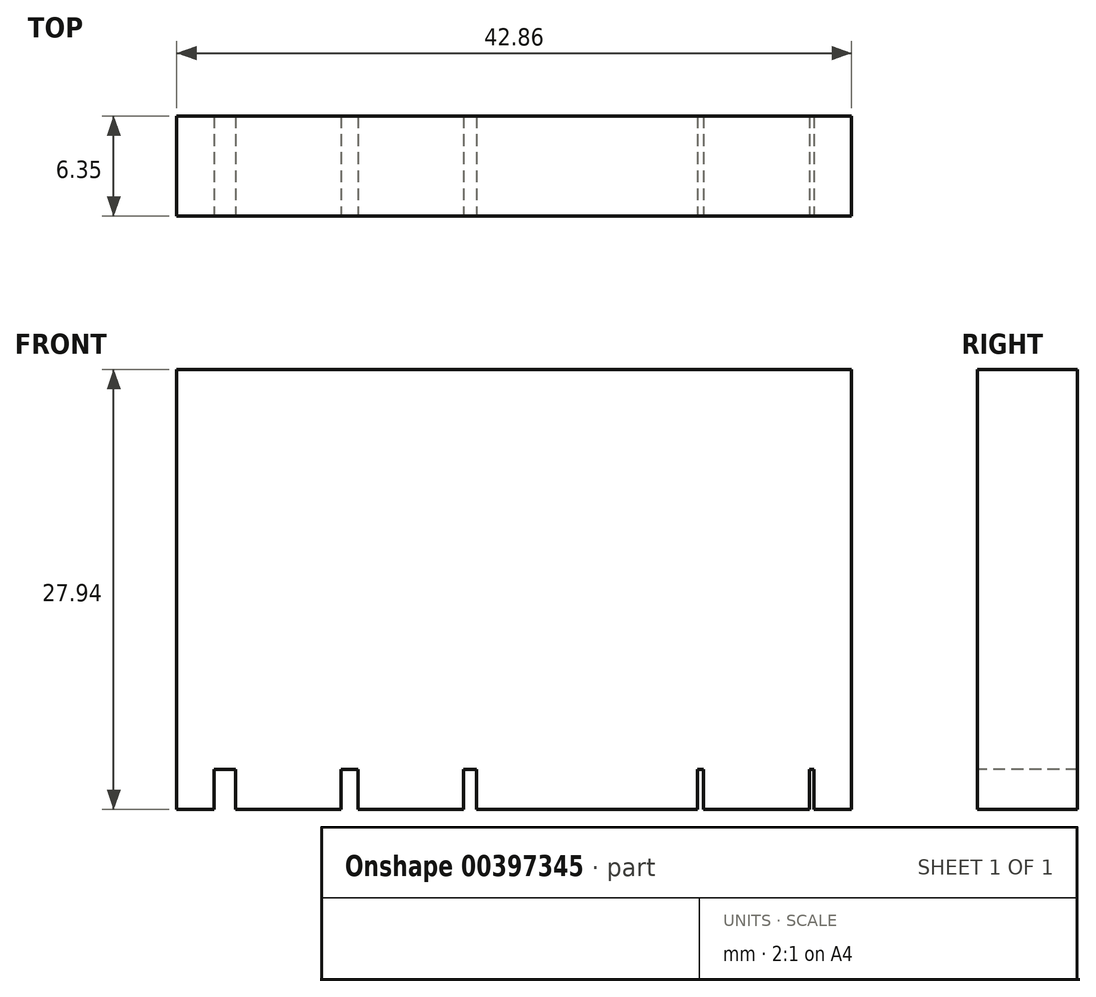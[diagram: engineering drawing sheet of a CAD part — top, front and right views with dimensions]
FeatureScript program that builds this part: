
annotation { "Feature Type Name" : "Feature", "Feature Type Description" : "" }
export const myFeature = defineFeature(function(context is Context, id is Id, definition is map)
    precondition{}
    {
        {
            var Q0;
            Q0=qCreatedBy(makeId("Top.planeOp"),FACE);
            var sketch = newSketch(context, id + "F0", { "sketchPlane" : qUnion([Q0])});
            skLineSegment(sketch, "E0", {"start": v(-23.52, 0) * mm, "end": v(19.34, 0) * mm});
            skLineSegment(sketch, "E1", {"start": v(19.34, 0) * mm, "end": v(19.34, -6.35) * mm});
            skLineSegment(sketch, "E2", {"start": v(19.34, -6.35) * mm, "end": v(-23.52, -6.35) * mm});
            skLineSegment(sketch, "E3", {"start": v(-23.52, -6.35) * mm, "end": v(-23.52, 0) * mm});
            skLineSegment(sketch, "E4", {"start": v(-21.14, 0) * mm, "end": v(-21.14, -6.35) * mm});
            skLineSegment(sketch, "E5", {"start": v(-19.8, 0) * mm, "end": v(-19.8, -6.35) * mm});
            skLineSegment(sketch, "E6", {"start": v(-13.08, 0) * mm, "end": v(-13.08, -6.35) * mm});
            skLineSegment(sketch, "E7", {"start": v(-12.01, 0) * mm, "end": v(-12.01, -6.35) * mm});
            skLineSegment(sketch, "E8", {"start": v(-4.5, 0) * mm, "end": v(-4.5, -6.35) * mm});
            skLineSegment(sketch, "E9", {"start": v(-5.3, 0) * mm, "end": v(-5.3, -6.35) * mm});
            skLineSegment(sketch, "E10", {"start": v(2.83, 0) * mm, "end": v(2.83, -6.35) * mm});
            skLineSegment(sketch, "E11", {"start": v(2.22, 0) * mm, "end": v(2.22, -6.35) * mm});
            skLineSegment(sketch, "E12", {"start": v(9.54, 0) * mm, "end": v(9.54, -6.35) * mm});
            skLineSegment(sketch, "E13", {"start": v(9.95, 0) * mm, "end": v(9.95, -6.35) * mm});
            skLineSegment(sketch, "E14", {"start": v(16.66, 0) * mm, "end": v(16.66, -6.35) * mm});
            skLineSegment(sketch, "E15", {"start": v(16.96, 0) * mm, "end": v(16.96, -6.35) * mm});
            skSolve(sketch);
        }
        {
            var Q0;
            {var subQ0=sQuery(id+"F0.wireOp",EDGE,"E3");Q0=makeQuery(id+"F0.imprint","IMPRINT",FACE,{"disambiguationData":[TD([[makeQuery(id+"F0.imprint","IMPRINT",EDGE,{"derivedFrom":subQ0}),-1.0]])]});}
            var Q1;
            {var subQ0=sQuery(id+"F0.wireOp",EDGE,"E1");Q1=makeQuery(id+"F0.imprint","IMPRINT",FACE,{"disambiguationData":[TD([[makeQuery(id+"F0.imprint","IMPRINT",EDGE,{"derivedFrom":subQ0}),-1.0]])]});}
            var Q2;
            {var subQ0=sQuery(id+"F0.wireOp",EDGE,"E4");Q2=makeQuery(id+"F0.imprint","IMPRINT",FACE,{"disambiguationData":[TD([[makeQuery(id+"F0.imprint","IMPRINT",EDGE,{"derivedFrom":subQ0}),1.0]])]});}
            var Q3;
            {var subQ0=sQuery(id+"F0.wireOp",EDGE,"E5");Q3=makeQuery(id+"F0.imprint","IMPRINT",FACE,{"disambiguationData":[TD([[makeQuery(id+"F0.imprint","IMPRINT",EDGE,{"derivedFrom":subQ0}),1.0]])]});}
            var Q4;
            {var subQ0=sQuery(id+"F0.wireOp",EDGE,"E6");Q4=makeQuery(id+"F0.imprint","IMPRINT",FACE,{"disambiguationData":[TD([[makeQuery(id+"F0.imprint","IMPRINT",EDGE,{"derivedFrom":subQ0}),1.0]])]});}
            var Q5;
            {var subQ0=sQuery(id+"F0.wireOp",EDGE,"E7");Q5=makeQuery(id+"F0.imprint","IMPRINT",FACE,{"disambiguationData":[TD([[makeQuery(id+"F0.imprint","IMPRINT",EDGE,{"derivedFrom":subQ0}),1.0]])]});}
            var Q6;
            {var subQ0=sQuery(id+"F0.wireOp",EDGE,"E8");Q6=makeQuery(id+"F0.imprint","IMPRINT",FACE,{"disambiguationData":[TD([[makeQuery(id+"F0.imprint","IMPRINT",EDGE,{"derivedFrom":subQ0}),-1.0]])]});}
            var Q7;
            {var subQ0=sQuery(id+"F0.wireOp",EDGE,"E8");Q7=makeQuery(id+"F0.imprint","IMPRINT",FACE,{"disambiguationData":[TD([[makeQuery(id+"F0.imprint","IMPRINT",EDGE,{"derivedFrom":subQ0}),1.0]])]});}
            var Q8;
            {var subQ0=sQuery(id+"F0.wireOp",EDGE,"E10");Q8=makeQuery(id+"F0.imprint","IMPRINT",FACE,{"disambiguationData":[TD([[makeQuery(id+"F0.imprint","IMPRINT",EDGE,{"derivedFrom":subQ0}),-1.0]])]});}
            var Q9;
            {var subQ0=sQuery(id+"F0.wireOp",EDGE,"E10");Q9=makeQuery(id+"F0.imprint","IMPRINT",FACE,{"disambiguationData":[TD([[makeQuery(id+"F0.imprint","IMPRINT",EDGE,{"derivedFrom":subQ0}),1.0]])]});}
            var Q10;
            {var subQ0=sQuery(id+"F0.wireOp",EDGE,"E12");Q10=makeQuery(id+"F0.imprint","IMPRINT",FACE,{"disambiguationData":[TD([[makeQuery(id+"F0.imprint","IMPRINT",EDGE,{"derivedFrom":subQ0}),1.0]])]});}
            var Q11;
            {var subQ0=sQuery(id+"F0.wireOp",EDGE,"E13");Q11=makeQuery(id+"F0.imprint","IMPRINT",FACE,{"disambiguationData":[TD([[makeQuery(id+"F0.imprint","IMPRINT",EDGE,{"derivedFrom":subQ0}),1.0]])]});}
            var Q12;
            {var subQ0=sQuery(id+"F0.wireOp",EDGE,"E14");Q12=makeQuery(id+"F0.imprint","IMPRINT",FACE,{"disambiguationData":[TD([[makeQuery(id+"F0.imprint","IMPRINT",EDGE,{"derivedFrom":subQ0}),1.0]])]});}
            extrude(context, id + "F1", {"entities" : qUnion([Q0, Q1, Q2, Q3, Q4, Q5, Q6, Q7, Q8, Q9, Q10, Q11, Q12]), "depth" : 25.4 * mm});
        }
        {
            var Q0;
            {var subQ0=sQuery(id+"F0.wireOp",EDGE,"E3");Q0=makeQuery(id+"F0.imprint","IMPRINT",FACE,{"disambiguationData":[TD([[makeQuery(id+"F0.imprint","IMPRINT",EDGE,{"derivedFrom":subQ0}),-1.0]])]});}
            var Q1;
            {var subQ0=sQuery(id+"F0.wireOp",EDGE,"E5");Q1=makeQuery(id+"F0.imprint","IMPRINT",FACE,{"disambiguationData":[TD([[makeQuery(id+"F0.imprint","IMPRINT",EDGE,{"derivedFrom":subQ0}),1.0]])]});}
            var Q2;
            {var subQ0=sQuery(id+"F0.wireOp",EDGE,"E7");Q2=makeQuery(id+"F0.imprint","IMPRINT",FACE,{"disambiguationData":[TD([[makeQuery(id+"F0.imprint","IMPRINT",EDGE,{"derivedFrom":subQ0}),1.0]])]});}
            var Q3;
            {var subQ0=sQuery(id+"F0.wireOp",EDGE,"E8");Q3=makeQuery(id+"F0.imprint","IMPRINT",FACE,{"disambiguationData":[TD([[makeQuery(id+"F0.imprint","IMPRINT",EDGE,{"derivedFrom":subQ0}),1.0]])]});}
            var Q4;
            {var subQ0=sQuery(id+"F0.wireOp",EDGE,"E10");Q4=makeQuery(id+"F0.imprint","IMPRINT",FACE,{"disambiguationData":[TD([[makeQuery(id+"F0.imprint","IMPRINT",EDGE,{"derivedFrom":subQ0}),1.0]])]});}
            var Q5;
            {var subQ0=sQuery(id+"F0.wireOp",EDGE,"E13");Q5=makeQuery(id+"F0.imprint","IMPRINT",FACE,{"disambiguationData":[TD([[makeQuery(id+"F0.imprint","IMPRINT",EDGE,{"derivedFrom":subQ0}),1.0]])]});}
            var Q6;
            {var subQ0=sQuery(id+"F0.wireOp",EDGE,"E1");Q6=makeQuery(id+"F0.imprint","IMPRINT",FACE,{"disambiguationData":[TD([[makeQuery(id+"F0.imprint","IMPRINT",EDGE,{"derivedFrom":subQ0}),-1.0]])]});}
            extrude(context, id + "F2", {"entities" : qUnion([Q0, Q1, Q2, Q3, Q4, Q5, Q6]), "operationType" : NewBodyOperationType.ADD, "oppositeDirection" : true, "depth" : 2.54 * mm});
        }
    });
